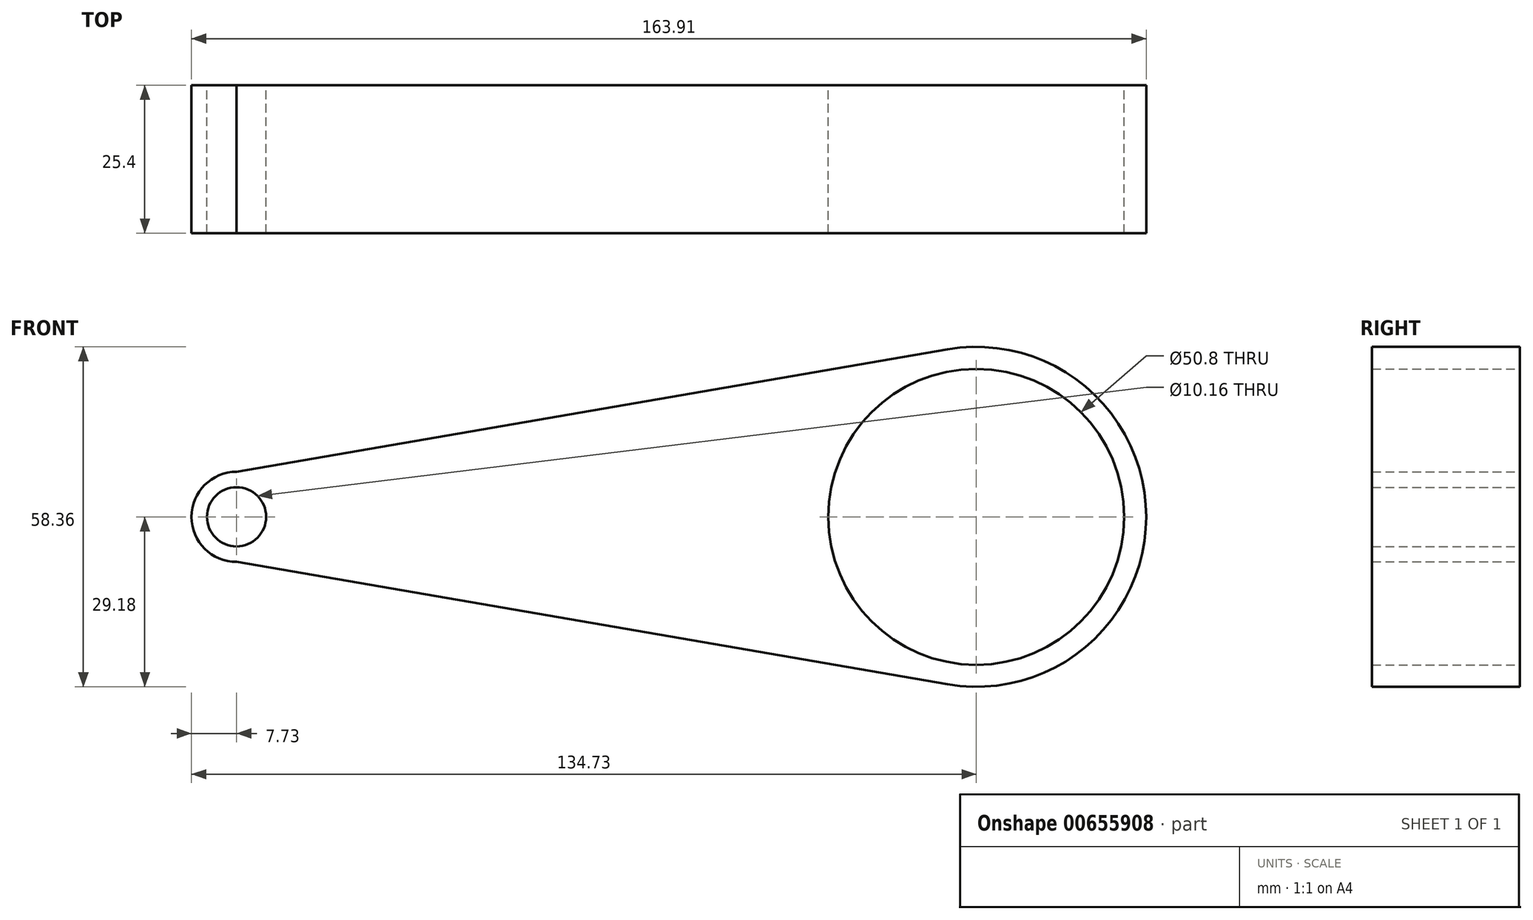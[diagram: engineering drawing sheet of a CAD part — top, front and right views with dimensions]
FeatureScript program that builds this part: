
annotation { "Feature Type Name" : "Feature", "Feature Type Description" : "" }
export const myFeature = defineFeature(function(context is Context, id is Id, definition is map)
    precondition{}
    {
        {
            var Q0;
            Q0=qCreatedBy(makeId("Front.planeOp"),FACE);
            var sketch = newSketch(context, id + "F0", { "sketchPlane" : qUnion([Q0])});
            skCircle(sketch, "E0", {"center": v(0, 0) * mm, "radius": 7.73 * mm});
            skCircle(sketch, "E1", {"center": v(127, 0) * mm, "radius": 29.18 * mm});
            skLineSegment(sketch, "E2", {"start": v(0, 7.73) * mm, "end": v(122.05, 28.75) * mm});
            skLineSegment(sketch, "E3", {"start": v(0, -7.73) * mm, "end": v(122.05, -28.75) * mm});
            skCircle(sketch, "E4", {"center": v(127, 0) * mm, "radius": 25.4 * mm});
            skCircle(sketch, "E5", {"center": v(0, 0) * mm, "radius": 5.08 * mm});
            skSolve(sketch);
        }
        {
            var Q0;
            Q0=makeQuery(id+"F0.imprint","IMPRINT",FACE,{"disambiguationData":[TD([[makeQuery(id+"F0.imprint","IMPRINT",EDGE,{"derivedFrom":sQuery(id+"F0.wireOp",EDGE,"E4")}),-1.0]])]});
            var Q1;
            {var subQ0=sQuery(id+"F0.wireOp",EDGE,"E2");Q1=makeQuery(id+"F0.imprint","IMPRINT",FACE,{"disambiguationData":[TD([[makeQuery(id+"F0.imprint","IMPRINT",EDGE,{"derivedFrom":subQ0}),-1.0]])]});}
            var Q2;
            Q2=makeQuery(id+"F0.imprint","IMPRINT",FACE,{"disambiguationData":[TD([[makeQuery(id+"F0.imprint","IMPRINT",EDGE,{"derivedFrom":sQuery(id+"F0.wireOp",EDGE,"E5")}),-1.0]])]});
            extrude(context, id + "F1", {"entities" : qUnion([Q0, Q1, Q2]), "depth" : 25.4 * mm, "offsetDistance" : 25.4 * mm});
        }
    });
